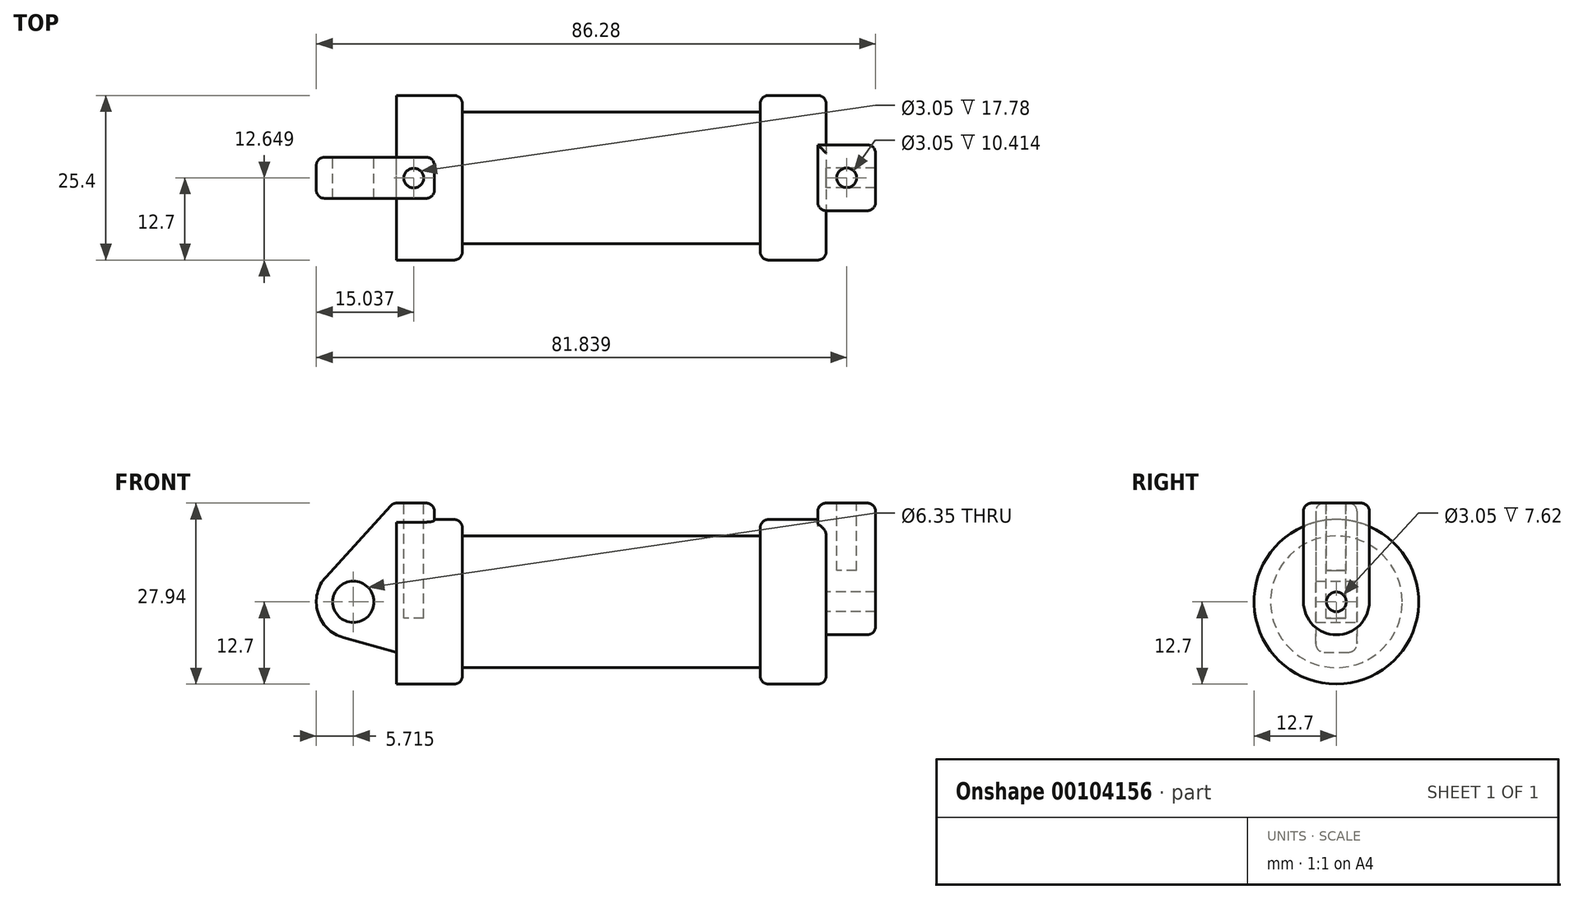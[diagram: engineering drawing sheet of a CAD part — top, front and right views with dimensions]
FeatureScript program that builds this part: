
annotation { "Feature Type Name" : "Feature", "Feature Type Description" : "" }
export const myFeature = defineFeature(function(context is Context, id is Id, definition is map)
    precondition{}
    {
        {
            var Q0;
            Q0=qCreatedBy(makeId("Front.planeOp"),FACE);
            var sketch = newSketch(context, id + "F0", { "sketchPlane" : qUnion([Q0])});
            skLineSegment(sketch, "E0", {"start": v(0, 0) * mm, "end": v(0, 12.7) * mm});
            skLineSegment(sketch, "E1", {"start": v(0, 12.7) * mm, "end": v(10.16, 12.7) * mm});
            skLineSegment(sketch, "E2", {"start": v(10.16, 12.7) * mm, "end": v(10.16, 10.16) * mm});
            skLineSegment(sketch, "E3", {"start": v(10.16, 10.16) * mm, "end": v(56.13, 10.16) * mm});
            skLineSegment(sketch, "E4", {"start": v(56.13, 10.16) * mm, "end": v(56.13, 12.7) * mm});
            skLineSegment(sketch, "E5", {"start": v(56.13, 12.7) * mm, "end": v(66.3, 12.7) * mm});
            skLineSegment(sketch, "E6", {"start": v(66.3, 12.7) * mm, "end": v(66.3, 0) * mm});
            skLineSegment(sketch, "E7", {"start": v(66.3, 0) * mm, "end": v(0, 0) * mm});
            skLineSegment(sketch, "E8", {"start": v(5.84, 15.24) * mm, "end": v(-0.5, 15.24) * mm});
            skLineSegment(sketch, "E9", {"start": v(-0.5, 15.24) * mm, "end": v(-10.88, 3.85) * mm});
            skLineSegment(sketch, "E10", {"start": v(0, 0) * mm, "end": v(-6.65, 0) * mm});
            skCircle(sketch, "E11", {"center": v(-6.65, 0) * mm, "radius": 5.72 * mm});
            skCircle(sketch, "E12", {"center": v(-6.65, 0) * mm, "radius": 3.18 * mm});
            skLineSegment(sketch, "E13", {"start": v(5.84, 15.24) * mm, "end": v(5.84, -9.4) * mm});
            skLineSegment(sketch, "E14", {"start": v(5.84, -9.4) * mm, "end": v(-8.18, -5.5) * mm});
            skSolve(sketch);
        }
        {
            var Q0;
            {var subQ0=sQuery(id+"F0.wireOp",EDGE,"E2");Q0=makeQuery(id+"F0.imprint","IMPRINT",FACE,{"disambiguationData":[TD([[makeQuery(id+"F0.imprint","IMPRINT",EDGE,{"derivedFrom":subQ0}),-1.0]])]});}
            var Q1;
            {var subQ0=sQuery(id+"F0.wireOp",EDGE,"E0");Q1=makeQuery(id+"F0.imprint","IMPRINT",FACE,{"disambiguationData":[TD([[makeQuery(id+"F0.imprint","IMPRINT",EDGE,{"derivedFrom":subQ0}),-1.0]])]});}
            var Q2;
            Q2=sQuery(id+"F0.wireOp",EDGE,"E7");
            revolve(context, id + "F1", {"entities" : qUnion([Q0, Q1]), "axis" : qUnion([Q2]), "revolveType" : RevolveType.FULL});
        }
        {
            var Q0;
            {var subQ3=sQuery(id+"F0.wireOp",EDGE,"E0");Q0=makeQuery(id+"F0.imprint","IMPRINT",FACE,{"disambiguationData":[TD([[makeQuery(id+"F0.imprint","IMPRINT",EDGE,{"derivedFrom":subQ3}),1.0]])]});}
            var Q1;
            {var subQ4=sQuery(id+"F0.wireOp",EDGE,"E12");Q1=makeQuery(id+"F0.imprint","IMPRINT",FACE,{"disambiguationData":[TD([[makeQuery(id+"F0.imprint","IMPRINT",EDGE,{"derivedFrom":subQ4}),-1.0]])]});}
            var Q2;
            {var subQ0=sQuery(id+"F0.wireOp",EDGE,"E14");Q2=makeQuery(id+"F0.imprint","IMPRINT",FACE,{"disambiguationData":[TD([[makeQuery(id+"F0.imprint","IMPRINT",EDGE,{"derivedFrom":subQ0}),-1.0]])]});}
            var Q3;
            {var subQ0=sQuery(id+"F0.wireOp",EDGE,"E0");Q3=makeQuery(id+"F0.imprint","IMPRINT",FACE,{"disambiguationData":[TD([[makeQuery(id+"F0.imprint","IMPRINT",EDGE,{"derivedFrom":subQ0}),-1.0]])]});}
            extrude(context, id + "F2", {"entities" : qUnion([Q0, Q1, Q2, Q3]), "operationType" : NewBodyOperationType.ADD, "endBound" : BoundingType.SYMMETRIC, "depth" : 6.35 * mm});
        }
        {
            var Q0;
            Q0=makeQuery(id+"F1.opRevolve","SWEPT_FACE",FACE,{"disambiguationData":[OSD([sQuery(id+"F0.wireOp",EDGE,"E6")])]});
            var sketch = newSketch(context, id + "F3", { "sketchPlane" : qUnion([Q0])});
            skCircle(sketch, "E15", {"center": v(0, 0) * mm, "radius": 5.08 * mm});
            skCircle(sketch, "E16", {"center": v(0, 0) * mm, "radius": 1.52 * mm});
            skLineSegment(sketch, "E17", {"start": v(5.08, 0) * mm, "end": v(5.08, 15.24) * mm});
            skLineSegment(sketch, "E18", {"start": v(-5.08, 0) * mm, "end": v(-5.08, 15.24) * mm});
            skLineSegment(sketch, "E19", {"start": v(-5.08, 15.24) * mm, "end": v(5.08, 15.24) * mm});
            skSolve(sketch);
        }
        {
            var Q0;
            Q0=makeQuery(id+"F3.imprint","IMPRINT",FACE,{"disambiguationData":[TD([[makeQuery(id+"F3.imprint","IMPRINT",EDGE,{"derivedFrom":sQuery(id+"F3.wireOp",EDGE,"E16")}),-1.0]])]});
            var Q1;
            {var subQ0=sQuery(id+"F3.wireOp",EDGE,"E17");var subQ1=sQuery(id+"F3.wireOp",EDGE,"E15");var subQ2=makeQuery(id+"F3.imprint","INTERSECT",VERTEX,{"derivedFrom":[subQ1,subQ0]});Q1=makeQuery(id+"F3.imprint","IMPRINT",FACE,{"disambiguationData":[TD([[makeQuery(id+"F3.imprint","IMPRINT",EDGE,{"disambiguationData":[TD([[subQ2,-1.0]])],"derivedFrom":subQ1}),-1.0]])]});}
            var Q2;
            {var subQ0=sQuery(id+"F3.wireOp",EDGE,"E19");Q2=makeQuery(id+"F3.imprint","IMPRINT",FACE,{"disambiguationData":[TD([[makeQuery(id+"F3.imprint","IMPRINT",EDGE,{"derivedFrom":subQ0}),-1.0]])]});}
            extrude(context, id + "F4", {"entities" : qUnion([Q0, Q1, Q2]), "operationType" : NewBodyOperationType.ADD, "depth" : 7.62 * mm, "hasSecondDirection" : true, "secondDirectionOppositeDirection" : true, "secondDirectionDepth" : 1.27 * mm});
        }
        {
            var Q0;
            Q0=makeQuery(id+"F4.opExtrude","SWEPT_FACE",FACE,{"disambiguationData":[OSD([sQuery(id+"F3.wireOp",EDGE,"E19")])]});
            var sketch = newSketch(context, id + "F5", { "sketchPlane" : qUnion([Q0])});
            skCircle(sketch, "E20", {"center": v(69.47, 0) * mm, "radius": 1.52 * mm});
            skSolve(sketch);
        }
        {
            var Q0;
            Q0=makeQuery(id+"F2.opExtrude","SWEPT_FACE",FACE,{"disambiguationData":[OSD([sQuery(id+"F0.wireOp",EDGE,"E8")])]});
            var sketch = newSketch(context, id + "F6", { "sketchPlane" : qUnion([Q0])});
            skCircle(sketch, "E21", {"center": v(2.67, -0.05) * mm, "radius": 1.52 * mm});
            skSolve(sketch);
        }
        {
            var Q0;
            Q0=makeQuery(id+"F6.imprint","IMPRINT",FACE,{"disambiguationData":[TD([[makeQuery(id+"F6.imprint","IMPRINT",EDGE,{"derivedFrom":sQuery(id+"F6.wireOp",EDGE,"E21")}),1.0]])]});
            extrude(context, id + "F7", {"entities" : qUnion([Q0]), "operationType" : NewBodyOperationType.REMOVE, "oppositeDirection" : true, "depth" : 17.78 * mm});
        }
        {
            var Q0;
            Q0=makeQuery(id+"F5.imprint","IMPRINT",FACE,{"disambiguationData":[TD([[makeQuery(id+"F5.imprint","IMPRINT",EDGE,{"derivedFrom":sQuery(id+"F5.wireOp",EDGE,"E20")}),1.0]])]});
            extrude(context, id + "F8", {"entities" : qUnion([Q0]), "operationType" : NewBodyOperationType.REMOVE, "oppositeDirection" : true, "depth" : 10.4 * mm});
        }
        {
            var Q0;
            Q0=makeQuery(id+"FQa9Bz3ZPIk9WfF_1.opRevolve","SWEPT_EDGE",EDGE,{"disambiguationData":[OSD([sQuery(id+"F0.wireOp",EDGE,"E0"),sQuery(id+"F0.wireOp",EDGE,"E1")])]});
            var Q1;
            Q1=makeQuery(id+"F1.opRevolve","SWEPT_EDGE",EDGE,{"disambiguationData":[OSD([sQuery(id+"F0.wireOp",EDGE,"E1"),sQuery(id+"F0.wireOp",EDGE,"E2")])]});
            var Q2;
            Q2=makeQuery(id+"F1.opRevolve","SWEPT_EDGE",EDGE,{"disambiguationData":[OSD([sQuery(id+"F0.wireOp",EDGE,"E4"),sQuery(id+"F0.wireOp",EDGE,"E5")])]});
            var Q3;
            Q3=makeQuery(id+"F1.opRevolve","SWEPT_EDGE",EDGE,{"disambiguationData":[OSD([sQuery(id+"F0.wireOp",EDGE,"E5"),sQuery(id+"F0.wireOp",EDGE,"E6")])]});
            fillet(context, id + "F9", {"entities" : qUnion([Q0, Q1, Q2, Q3]), "radius" : 1.27 * mm, "tangentPropagation" : true, "allowEdgeOverflow" : false});
        }
        {
            var Q0;
            Q0=makeQuery(id+"F2.opExtrude","CAP_EDGE",EDGE,{"disambiguationData":[OSD([sQuery(id+"F0.wireOp",EDGE,"E8")])],"isStart":false});
            var Q1;
            Q1=makeQuery(id+"F2.opExtrude","CAP_EDGE",EDGE,{"disambiguationData":[OSD([sQuery(id+"F0.wireOp",EDGE,"E8")])],"isStart":true});
            var Q2;
            Q2=makeQuery(id+"F2.opExtrude","SWEPT_EDGE",EDGE,{"disambiguationData":[OSD([sQuery(id+"F0.wireOp",EDGE,"E8"),sQuery(id+"F0.wireOp",EDGE,"E9")])]});
            var Q3;
            Q3=makeQuery(id+"F2.opExtrude","CAP_EDGE",EDGE,{"disambiguationData":[OSD([sQuery(id+"F0.wireOp",EDGE,"E9")])],"isStart":false});
            var Q4;
            Q4=makeQuery(id+"F2.opExtrude","CAP_EDGE",EDGE,{"disambiguationData":[OSD([sQuery(id+"F0.wireOp",EDGE,"E9")])],"isStart":true});
            var Q5;
            Q5=makeQuery(id+"F2.opExtrude","CAP_EDGE",EDGE,{"disambiguationData":[OSD([sQuery(id+"F0.wireOp",EDGE,"E11")])],"isStart":false});
            var Q6;
            Q6=makeQuery(id+"F2.opExtrude","CAP_EDGE",EDGE,{"disambiguationData":[OSD([sQuery(id+"F0.wireOp",EDGE,"E11")])],"isStart":true});
            var Q7;
            Q7=makeQuery(id+"F2.opExtrude","CAP_EDGE",EDGE,{"disambiguationData":[OSD([sQuery(id+"F0.wireOp",EDGE,"E14")])],"isStart":false});
            var Q8;
            Q8=makeQuery(id+"F2.opExtrude","CAP_EDGE",EDGE,{"disambiguationData":[OSD([sQuery(id+"F0.wireOp",EDGE,"E14")])],"isStart":true});
            var Q9;
            Q9=makeQuery(id+"F2.opExtrude","SWEPT_EDGE",EDGE,{"disambiguationData":[OSD([sQuery(id+"F0.wireOp",EDGE,"E8"),sQuery(id+"F0.wireOp",EDGE,"E13")])]});
            var Q10;
            Q10=makeQuery(id+"F2.opExtrude","SWEPT_EDGE",EDGE,{"disambiguationData":[OSD([sQuery(id+"F0.wireOp",EDGE,"E1"),sQuery(id+"F0.wireOp",EDGE,"E13")])]});
            var Q11;
            {var subQ0=sQuery(id+"F0.wireOp",EDGE,"E13");Q11=makeQuery(id+"F2.opExtrude","CAP_EDGE",EDGE,{"disambiguationData":[OSD([subQ0]),TDD([makeQuery(id+"F0.imprint","IMPRINT",EDGE,{"disambiguationData":[TD([[makeQuery(id+"F0.imprint","INTERSECT",VERTEX,{"derivedFrom":[sQuery(id+"F0.wireOp",EDGE,"E8"),subQ0]}),-1.0]])],"derivedFrom":subQ0})])],"isStart":false});}
            var Q12;
            {var subQ0=sQuery(id+"F0.wireOp",EDGE,"E13");Q12=makeQuery(id+"F2.opExtrude","CAP_EDGE",EDGE,{"disambiguationData":[OSD([subQ0]),TDD([makeQuery(id+"F0.imprint","IMPRINT",EDGE,{"disambiguationData":[TD([[makeQuery(id+"F0.imprint","INTERSECT",VERTEX,{"derivedFrom":[sQuery(id+"F0.wireOp",EDGE,"E8"),subQ0]}),-1.0]])],"derivedFrom":subQ0})])],"isStart":true});}
            fillet(context, id + "F10", {"entities" : qUnion([Q0, Q1, Q2, Q3, Q4, Q5, Q6, Q7, Q8, Q9, Q10, Q11, Q12]), "radius" : 1.27 * mm, "tangentPropagation" : true, "allowEdgeOverflow" : false});
        }
        {
            var Q0;
            Q0=makeQuery(id+"F4.opExtrude","CAP_EDGE",EDGE,{"disambiguationData":[OSD([sQuery(id+"F3.wireOp",EDGE,"E19")])],"isStart":true});
            var Q1;
            Q1=makeQuery(id+"F4.opExtrude","SWEPT_EDGE",EDGE,{"disambiguationData":[OSD([sQuery(id+"F3.wireOp",EDGE,"E18"),sQuery(id+"F3.wireOp",EDGE,"E19")])]});
            var Q2;
            Q2=makeQuery(id+"F4.opExtrude","SWEPT_EDGE",EDGE,{"disambiguationData":[OSD([sQuery(id+"F3.wireOp",EDGE,"E17"),sQuery(id+"F3.wireOp",EDGE,"E19")])]});
            var Q3;
            Q3=makeQuery(id+"F4.opExtrude","CAP_EDGE",EDGE,{"disambiguationData":[OSD([sQuery(id+"F3.wireOp",EDGE,"E19")])],"isStart":false});
            var Q4;
            Q4=makeQuery(id+"F4.opExtrude","CAP_EDGE",EDGE,{"disambiguationData":[OSD([sQuery(id+"F3.wireOp",EDGE,"E18")])],"isStart":false});
            var Q5;
            Q5=makeQuery(id+"F4.opExtrude","CAP_EDGE",EDGE,{"disambiguationData":[OSD([sQuery(id+"F3.wireOp",EDGE,"E18")])],"isStart":true});
            var Q6;
            Q6=makeQuery(id+"F4.opExtrude","CAP_EDGE",EDGE,{"disambiguationData":[OSD([sQuery(id+"F3.wireOp",EDGE,"E17")])],"isStart":false});
            var Q7;
            Q7=makeQuery(id+"F4.opExtrude","CAP_EDGE",EDGE,{"disambiguationData":[OSD([sQuery(id+"F3.wireOp",EDGE,"E15")])],"isStart":false});
            var Q8;
            Q8=makeQuery(id+"F4.opExtrude","SWEPT_EDGE",EDGE,{"disambiguationData":[OSD([sQuery(id+"F3.wireOp",EDGE,"E15"),sQuery(id+"F3.wireOp",EDGE,"E17")])]});
            var Q9;
            Q9=makeQuery(id+"F4.opExtrude","SWEPT_EDGE",EDGE,{"disambiguationData":[OSD([sQuery(id+"F3.wireOp",EDGE,"E15"),sQuery(id+"F3.wireOp",EDGE,"E18")])]});
            fillet(context, id + "F11", {"entities" : qUnion([Q0, Q1, Q2, Q3, Q4, Q5, Q6, Q7, Q8, Q9]), "radius" : 1.27 * mm, "tangentPropagation" : true, "allowEdgeOverflow" : false});
        }
    });
